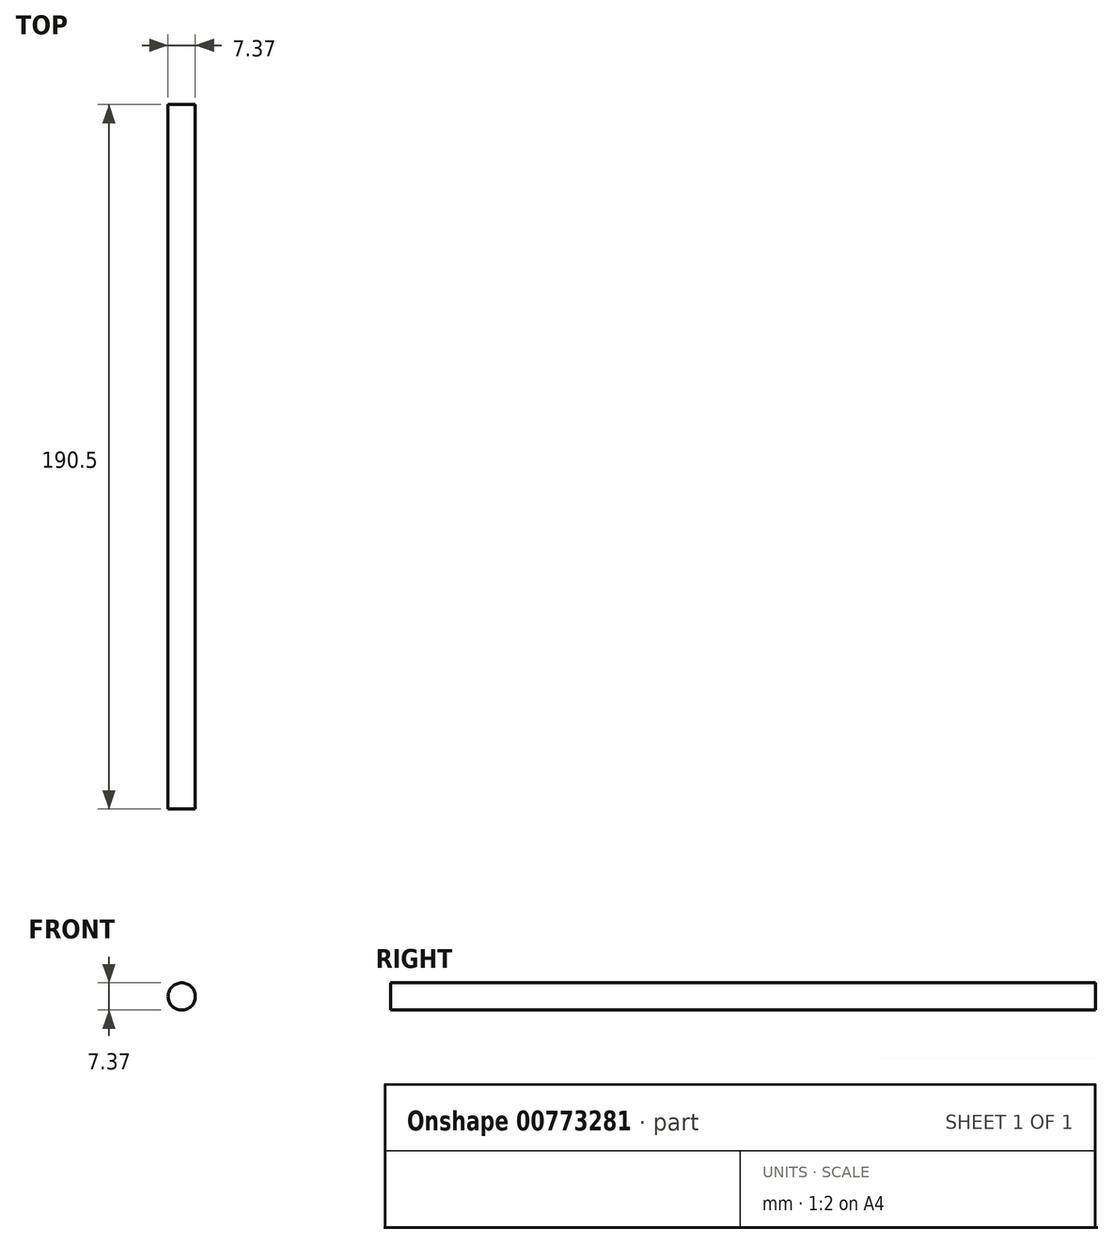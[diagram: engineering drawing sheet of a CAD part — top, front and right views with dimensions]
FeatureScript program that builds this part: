
annotation { "Feature Type Name" : "Feature", "Feature Type Description" : "" }
export const myFeature = defineFeature(function(context is Context, id is Id, definition is map)
    precondition{}
    {
        {
            var Q0;
            Q0=qCreatedBy(makeId("Front.planeOp"),FACE);
            var sketch = newSketch(context, id + "F0", { "sketchPlane" : qUnion([Q0])});
            skCircle(sketch, "E0", {"center": v(-40.38, 28) * mm, "radius": 3.68 * mm});
            skSolve(sketch);
        }
        {
            var Q0;
            Q0=qSketchRegion(id+"F0",true);
            extrude(context, id + "F1", {"entities" : qUnion([Q0]), "depth" : 190.5 * mm, "offsetDistance" : 25.4 * mm});
        }
    });
